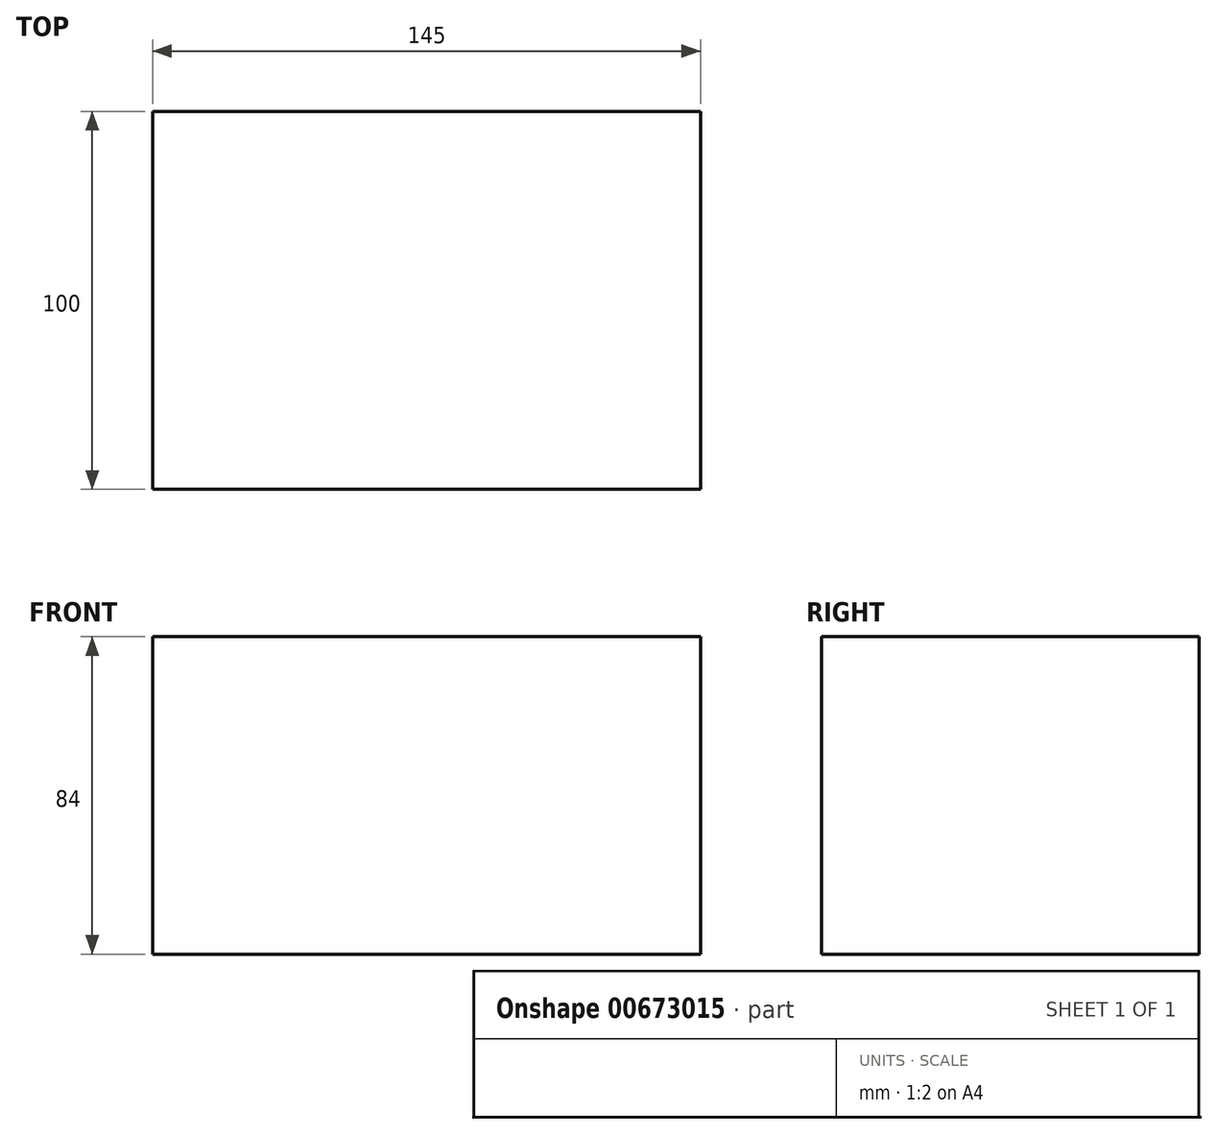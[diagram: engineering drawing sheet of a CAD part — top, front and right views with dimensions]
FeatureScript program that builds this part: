
annotation { "Feature Type Name" : "Feature", "Feature Type Description" : "" }
export const myFeature = defineFeature(function(context is Context, id is Id, definition is map)
    precondition{}
    {
        {
            var Q0;
            Q0=qCreatedBy(makeId("Front.planeOp"),FACE);
            var sketch = newSketch(context, id + "F0", { "sketchPlane" : qUnion([Q0])});
            skLineSegment(sketch, "E0.bottom", {"start": v(0, 0) * mm, "end": v(27.84, 0) * mm});
            skLineSegment(sketch, "E0.top", {"start": v(0, 24.96) * mm, "end": v(27.84, 24.96) * mm});
            skLineSegment(sketch, "E0.left", {"start": v(0, 0) * mm, "end": v(0, 24.96) * mm});
            skLineSegment(sketch, "E0.right", {"start": v(27.84, 0) * mm, "end": v(27.84, 24.96) * mm});
            skSolve(sketch);
        }
        {
            var Q0;
            Q0=makeQuery(id+"F0.imprint","IMPRINT",FACE,{"disambiguationData":[TD([[makeQuery(id+"F0.imprint","IMPRINT",EDGE,{"derivedFrom":sQuery(id+"F0.wireOp",EDGE,"E0.bottom")}),1.0]])]});
            extrude(context, id + "F1", {"entities" : qUnion([Q0]), "depth" : 145 * mm, "offsetDistance" : 25 * mm});
        }
        {
            var Q0;
            Q0=makeQuery(id+"F1.opExtrude","SWEPT_FACE",FACE,{"disambiguationData":[OSD([sQuery(id+"F0.wireOp",EDGE,"E0.left")])]});
            extrude(context, id + "F2", {"entities" : qUnion([Q0]), "operationType" : NewBodyOperationType.ADD, "oppositeDirection" : true, "depth" : 145 * mm, "offsetDistance" : 25 * mm});
        }
        {
            var Q0;
            {var subQ0=sQuery(id+"F0.wireOp",EDGE,"E0.bottom");Q0=makeQuery(id+"F2.boolean.opBoolean","MERGE",FACE,{"derivedFrom":[makeQuery(id+"F1.opExtrude","SWEPT_FACE",FACE,{"disambiguationData":[OSD([subQ0])]}),makeQuery(id+"F2.opExtrude","SWEPT_FACE",FACE,{"disambiguationData":[OSD([subQ0,sQuery(id+"F0.wireOp",EDGE,"E0.left")])]})]});}
            extrude(context, id + "F3", {"entities" : qUnion([Q0]), "operationType" : NewBodyOperationType.ADD, "oppositeDirection" : true, "depth" : 84 * mm, "offsetDistance" : 25 * mm});
        }
        {
            var Q0;
            {var subQ0=sQuery(id+"F0.wireOp",EDGE,"E0.left");var subQ1=sQuery(id+"F0.wireOp",EDGE,"E0.bottom");Q0=makeQuery(id+"F3.boolean.opBoolean","MERGE",FACE,{"derivedFrom":[makeQuery(id+"F2.boolean.opBoolean","MERGE",FACE,{"derivedFrom":[makeQuery(id+"F1.opExtrude","CAP_FACE",FACE,{"disambiguationData":[OSD([subQ1,sQuery(id+"F0.wireOp",EDGE,"E0.top"),subQ0,sQuery(id+"F0.wireOp",EDGE,"E0.right")])],"isStart":false}),makeQuery(id+"F2.opExtrude","SWEPT_FACE",FACE,{"disambiguationData":[OSD([subQ0]),TDD([makeQuery(id+"F1.opExtrude","CAP_EDGE",EDGE,{"disambiguationData":[OSD([subQ0])],"isStart":false})])]})]}),makeQuery(id+"F3.opExtrude","SWEPT_FACE",FACE,{"disambiguationData":[OSD([subQ1,subQ0]),TDD([makeQuery(id+"F2.boolean.opBoolean","MERGE",EDGE,{"derivedFrom":[makeQuery(id+"F1.opExtrude","CAP_EDGE",EDGE,{"disambiguationData":[OSD([subQ1])],"isStart":false}),makeQuery(id+"F2.opExtrude","SWEPT_EDGE",EDGE,{"disambiguationData":[OSD([subQ1,subQ0]),TDD([makeQuery(id+"F1.opExtrude","CAP_VERTEX",VERTEX,{"disambiguationData":[OSD([subQ1,subQ0])],"isStart":false})])]})]})])]})]});}
            extrude(context, id + "F4", {"entities" : qUnion([Q0]), "operationType" : NewBodyOperationType.REMOVE, "oppositeDirection" : true, "depth" : 45 * mm, "offsetDistance" : 25 * mm});
        }
    });
